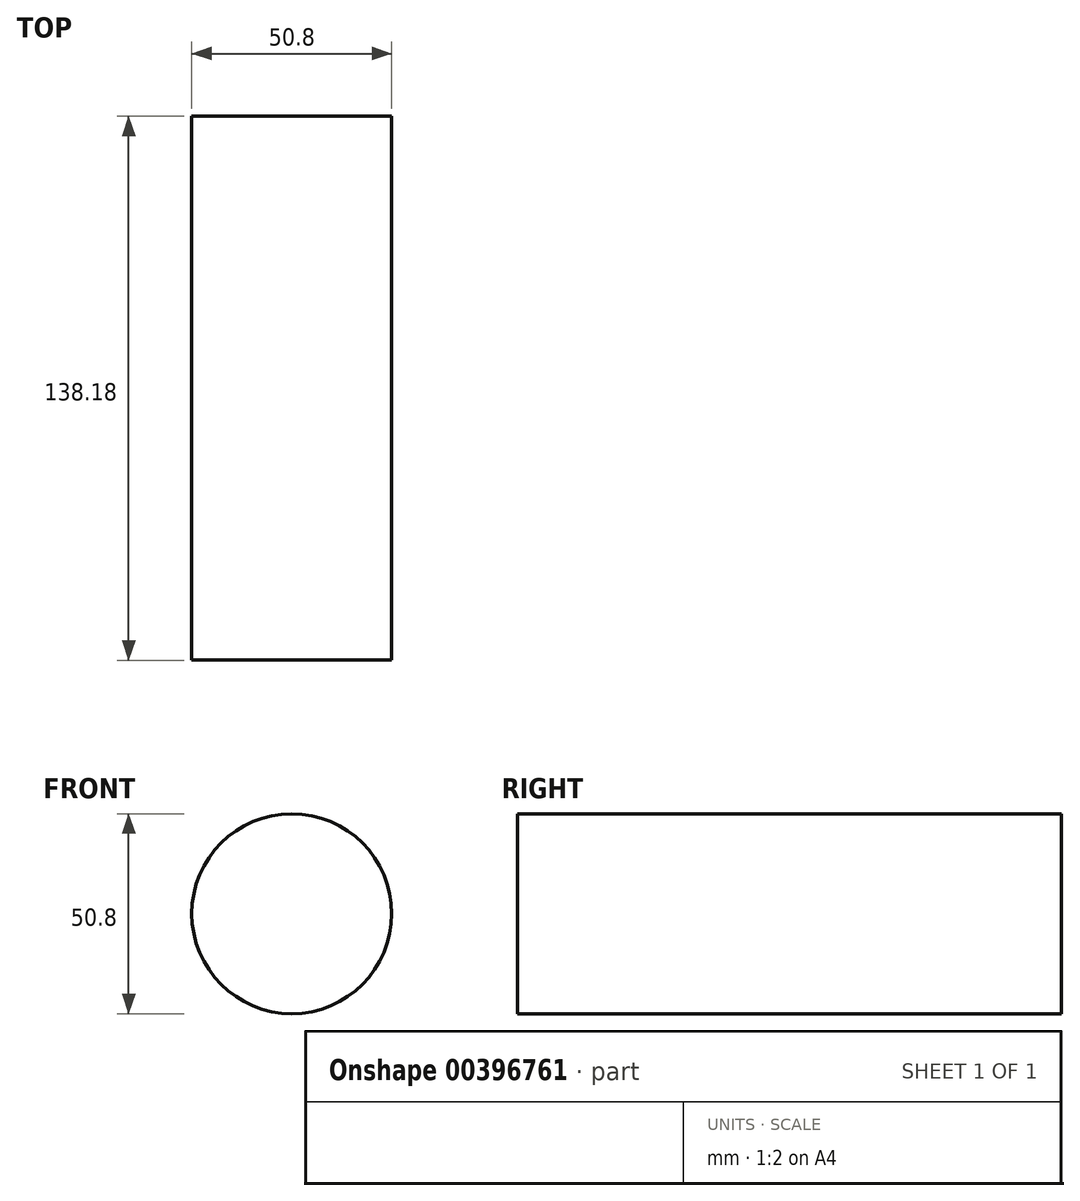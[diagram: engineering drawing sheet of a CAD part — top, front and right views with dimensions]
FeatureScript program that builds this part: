
annotation { "Feature Type Name" : "Feature", "Feature Type Description" : "" }
export const myFeature = defineFeature(function(context is Context, id is Id, definition is map)
    precondition{}
    {
        {
            var Q0;
            Q0=qCreatedBy(makeId("Front.planeOp"),FACE);
            var sketch = newSketch(context, id + "F0", { "sketchPlane" : qUnion([Q0])});
            skCircle(sketch, "E0", {"center": v(0, 0) * mm, "radius": 25.4 * mm});
            skSolve(sketch);
        }
        {
            var Q0;
            Q0=makeQuery(id+"F0.imprint","IMPRINT",FACE,{"disambiguationData":[TD([[makeQuery(id+"F0.imprint","IMPRINT",EDGE,{"derivedFrom":sQuery(id+"F0.wireOp",EDGE,"E0")}),1.0]])]});
            extrude(context, id + "F1", {"entities" : qUnion([Q0]), "depth" : 138.18 * mm});
        }
    });
